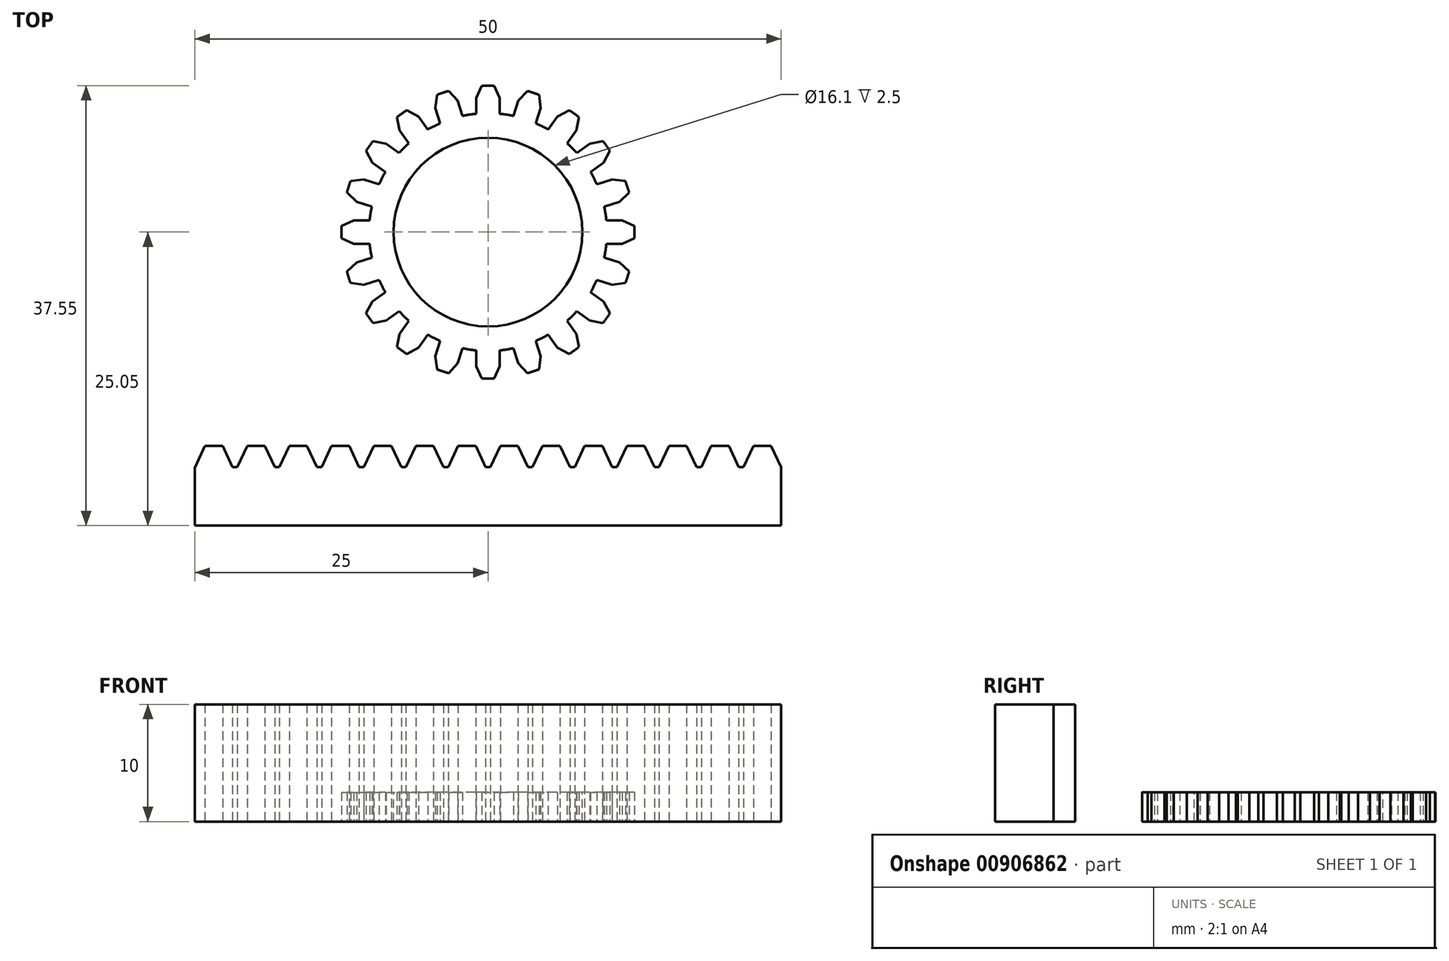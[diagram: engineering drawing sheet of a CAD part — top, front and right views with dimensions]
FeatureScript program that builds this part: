
annotation { "Feature Type Name" : "Feature", "Feature Type Description" : "" }
export const myFeature = defineFeature(function(context is Context, id is Id, definition is map)
    precondition{}
    {
        {
            var Q0;
            Q0=qCreatedBy(makeId("Top.planeOp"),FACE);
            var sketch = newSketch(context, id + "F0", { "sketchPlane" : qUnion([Q0])});
            skCircle(sketch, "E0", {"center": v(0, 0) * mm, "radius": 11.5 * mm, "construction": true});
            skLineSegment(sketch, "E1", {"start": v(-0.52, 12.49) * mm, "end": v(-1, 11.46) * mm});
            skLineSegment(sketch, "E2", {"start": v(-1, 11.46) * mm, "end": v(-1, 10.1) * mm});
            skLineSegment(sketch, "E3", {"start": v(-0.52, 15.02) * mm, "end": v(-0.52, 9.7) * mm, "construction": true});
            skLineSegment(sketch, "E4.MirrorCS", {"start": v(0.52, 12.49) * mm, "end": v(1, 11.46) * mm});
            skLineSegment(sketch, "E5.MirrorCS", {"start": v(1, 11.46) * mm, "end": v(1, 10.1) * mm});
            skArc(sketch, "E6", {"start": v(-0.52, 12.49) * mm, "mid": v(0, 12.5) * mm, "end": v(0.52, 12.49) * mm});
            skLineSegment(sketch, "E7.1.0", {"start": v(-4.5, 10.59) * mm, "end": v(-4.07, 9.3) * mm});
            skLineSegment(sketch, "E7.1.1", {"start": v(-3.37, 12.04) * mm, "end": v(-2.59, 11.2) * mm});
            skLineSegment(sketch, "E7.1.2", {"start": v(-2.59, 11.2) * mm, "end": v(-2.17, 9.91) * mm});
            skLineSegment(sketch, "E7.1.3", {"start": v(-4.35, 11.72) * mm, "end": v(-4.5, 10.59) * mm});
            skArc(sketch, "E7.1.4", {"start": v(-4.35, 11.72) * mm, "mid": v(-3.86, 11.89) * mm, "end": v(-3.37, 12.04) * mm});
            skLineSegment(sketch, "E7.2.0", {"start": v(-7.54, 8.68) * mm, "end": v(-6.74, 7.58) * mm});
            skLineSegment(sketch, "E7.2.1", {"start": v(-6.92, 10.4) * mm, "end": v(-5.92, 9.86) * mm});
            skLineSegment(sketch, "E7.2.2", {"start": v(-5.92, 9.86) * mm, "end": v(-5.13, 8.76) * mm});
            skLineSegment(sketch, "E7.2.3", {"start": v(-7.76, 9.8) * mm, "end": v(-7.54, 8.68) * mm});
            skArc(sketch, "E7.2.4", {"start": v(-7.76, 9.8) * mm, "mid": v(-7.35, 10.11) * mm, "end": v(-6.92, 10.4) * mm});
            skLineSegment(sketch, "E7.3.0", {"start": v(-9.86, 5.92) * mm, "end": v(-8.76, 5.13) * mm});
            skLineSegment(sketch, "E7.3.1", {"start": v(-9.8, 7.76) * mm, "end": v(-8.68, 7.54) * mm});
            skLineSegment(sketch, "E7.3.2", {"start": v(-8.68, 7.54) * mm, "end": v(-7.58, 6.74) * mm});
            skLineSegment(sketch, "E7.3.3", {"start": v(-10.4, 6.92) * mm, "end": v(-9.86, 5.92) * mm});
            skArc(sketch, "E7.3.4", {"start": v(-10.4, 6.92) * mm, "mid": v(-10.11, 7.35) * mm, "end": v(-9.8, 7.76) * mm});
            skLineSegment(sketch, "E7.4.0", {"start": v(-11.2, 2.59) * mm, "end": v(-9.91, 2.17) * mm});
            skLineSegment(sketch, "E7.4.1", {"start": v(-11.72, 4.35) * mm, "end": v(-10.59, 4.5) * mm});
            skLineSegment(sketch, "E7.4.2", {"start": v(-10.59, 4.5) * mm, "end": v(-9.3, 4.07) * mm});
            skLineSegment(sketch, "E7.4.3", {"start": v(-12.04, 3.37) * mm, "end": v(-11.2, 2.59) * mm});
            skArc(sketch, "E7.4.4", {"start": v(-12.04, 3.37) * mm, "mid": v(-11.89, 3.86) * mm, "end": v(-11.72, 4.35) * mm});
            skLineSegment(sketch, "E7.5.0", {"start": v(-11.46, -1) * mm, "end": v(-10.1, -1) * mm});
            skLineSegment(sketch, "E7.5.1", {"start": v(-12.49, 0.52) * mm, "end": v(-11.46, 1) * mm});
            skLineSegment(sketch, "E7.5.2", {"start": v(-11.46, 1) * mm, "end": v(-10.1, 1) * mm});
            skLineSegment(sketch, "E7.5.3", {"start": v(-12.49, -0.52) * mm, "end": v(-11.46, -1) * mm});
            skArc(sketch, "E7.5.4", {"start": v(-12.49, -0.52) * mm, "mid": v(-12.5, 0) * mm, "end": v(-12.49, 0.52) * mm});
            skLineSegment(sketch, "E7.6.0", {"start": v(-10.59, -4.5) * mm, "end": v(-9.3, -4.07) * mm});
            skLineSegment(sketch, "E7.6.1", {"start": v(-12.04, -3.37) * mm, "end": v(-11.2, -2.59) * mm});
            skLineSegment(sketch, "E7.6.2", {"start": v(-11.2, -2.59) * mm, "end": v(-9.91, -2.17) * mm});
            skLineSegment(sketch, "E7.6.3", {"start": v(-11.72, -4.35) * mm, "end": v(-10.59, -4.5) * mm});
            skArc(sketch, "E7.6.4", {"start": v(-11.72, -4.35) * mm, "mid": v(-11.89, -3.86) * mm, "end": v(-12.04, -3.37) * mm});
            skLineSegment(sketch, "E7.7.0", {"start": v(-8.68, -7.54) * mm, "end": v(-7.58, -6.74) * mm});
            skLineSegment(sketch, "E7.7.1", {"start": v(-10.4, -6.92) * mm, "end": v(-9.86, -5.92) * mm});
            skLineSegment(sketch, "E7.7.2", {"start": v(-9.86, -5.92) * mm, "end": v(-8.76, -5.13) * mm});
            skLineSegment(sketch, "E7.7.3", {"start": v(-9.8, -7.76) * mm, "end": v(-8.68, -7.54) * mm});
            skArc(sketch, "E7.7.4", {"start": v(-9.8, -7.76) * mm, "mid": v(-10.11, -7.35) * mm, "end": v(-10.4, -6.92) * mm});
            skLineSegment(sketch, "E7.8.0", {"start": v(-5.92, -9.86) * mm, "end": v(-5.13, -8.76) * mm});
            skLineSegment(sketch, "E7.8.1", {"start": v(-7.76, -9.8) * mm, "end": v(-7.54, -8.68) * mm});
            skLineSegment(sketch, "E7.8.2", {"start": v(-7.54, -8.68) * mm, "end": v(-6.74, -7.58) * mm});
            skLineSegment(sketch, "E7.8.3", {"start": v(-6.92, -10.4) * mm, "end": v(-5.92, -9.86) * mm});
            skArc(sketch, "E7.8.4", {"start": v(-6.92, -10.4) * mm, "mid": v(-7.35, -10.11) * mm, "end": v(-7.76, -9.8) * mm});
            skLineSegment(sketch, "E7.9.0", {"start": v(-2.59, -11.2) * mm, "end": v(-2.17, -9.91) * mm});
            skLineSegment(sketch, "E7.9.1", {"start": v(-4.35, -11.72) * mm, "end": v(-4.5, -10.59) * mm});
            skLineSegment(sketch, "E7.9.2", {"start": v(-4.5, -10.59) * mm, "end": v(-4.07, -9.3) * mm});
            skLineSegment(sketch, "E7.9.3", {"start": v(-3.37, -12.04) * mm, "end": v(-2.59, -11.2) * mm});
            skArc(sketch, "E7.9.4", {"start": v(-3.37, -12.04) * mm, "mid": v(-3.86, -11.89) * mm, "end": v(-4.35, -11.72) * mm});
            skLineSegment(sketch, "E7.10.0", {"start": v(1, -11.46) * mm, "end": v(1, -10.1) * mm});
            skLineSegment(sketch, "E7.10.1", {"start": v(-0.52, -12.49) * mm, "end": v(-1, -11.46) * mm});
            skLineSegment(sketch, "E7.10.2", {"start": v(-1, -11.46) * mm, "end": v(-1, -10.1) * mm});
            skLineSegment(sketch, "E7.10.3", {"start": v(0.52, -12.49) * mm, "end": v(1, -11.46) * mm});
            skArc(sketch, "E7.10.4", {"start": v(0.52, -12.49) * mm, "mid": v(0, -12.5) * mm, "end": v(-0.52, -12.49) * mm});
            skLineSegment(sketch, "E7.11.0", {"start": v(4.5, -10.59) * mm, "end": v(4.07, -9.3) * mm});
            skLineSegment(sketch, "E7.11.1", {"start": v(3.37, -12.04) * mm, "end": v(2.59, -11.2) * mm});
            skLineSegment(sketch, "E7.11.2", {"start": v(2.59, -11.2) * mm, "end": v(2.17, -9.91) * mm});
            skLineSegment(sketch, "E7.11.3", {"start": v(4.35, -11.72) * mm, "end": v(4.5, -10.59) * mm});
            skArc(sketch, "E7.11.4", {"start": v(4.35, -11.72) * mm, "mid": v(3.86, -11.89) * mm, "end": v(3.37, -12.04) * mm});
            skLineSegment(sketch, "E7.12.0", {"start": v(7.54, -8.68) * mm, "end": v(6.74, -7.58) * mm});
            skLineSegment(sketch, "E7.12.1", {"start": v(6.92, -10.4) * mm, "end": v(5.92, -9.86) * mm});
            skLineSegment(sketch, "E7.12.2", {"start": v(5.92, -9.86) * mm, "end": v(5.13, -8.76) * mm});
            skLineSegment(sketch, "E7.12.3", {"start": v(7.76, -9.8) * mm, "end": v(7.54, -8.68) * mm});
            skArc(sketch, "E7.12.4", {"start": v(7.76, -9.8) * mm, "mid": v(7.35, -10.11) * mm, "end": v(6.92, -10.4) * mm});
            skLineSegment(sketch, "E7.13.0", {"start": v(9.86, -5.92) * mm, "end": v(8.76, -5.13) * mm});
            skLineSegment(sketch, "E7.13.1", {"start": v(9.8, -7.76) * mm, "end": v(8.68, -7.54) * mm});
            skLineSegment(sketch, "E7.13.2", {"start": v(8.68, -7.54) * mm, "end": v(7.58, -6.74) * mm});
            skLineSegment(sketch, "E7.13.3", {"start": v(10.4, -6.92) * mm, "end": v(9.86, -5.92) * mm});
            skArc(sketch, "E7.13.4", {"start": v(10.4, -6.92) * mm, "mid": v(10.11, -7.35) * mm, "end": v(9.8, -7.76) * mm});
            skLineSegment(sketch, "E7.14.0", {"start": v(11.2, -2.59) * mm, "end": v(9.91, -2.17) * mm});
            skLineSegment(sketch, "E7.14.1", {"start": v(11.72, -4.35) * mm, "end": v(10.59, -4.5) * mm});
            skLineSegment(sketch, "E7.14.2", {"start": v(10.59, -4.5) * mm, "end": v(9.3, -4.07) * mm});
            skLineSegment(sketch, "E7.14.3", {"start": v(12.04, -3.37) * mm, "end": v(11.2, -2.59) * mm});
            skArc(sketch, "E7.14.4", {"start": v(12.04, -3.37) * mm, "mid": v(11.89, -3.86) * mm, "end": v(11.72, -4.35) * mm});
            skLineSegment(sketch, "E7.15.0", {"start": v(11.46, 1) * mm, "end": v(10.1, 1) * mm});
            skLineSegment(sketch, "E7.15.1", {"start": v(12.49, -0.52) * mm, "end": v(11.46, -1) * mm});
            skLineSegment(sketch, "E7.15.2", {"start": v(11.46, -1) * mm, "end": v(10.1, -1) * mm});
            skLineSegment(sketch, "E7.15.3", {"start": v(12.49, 0.52) * mm, "end": v(11.46, 1) * mm});
            skArc(sketch, "E7.15.4", {"start": v(12.49, 0.52) * mm, "mid": v(12.5, 0) * mm, "end": v(12.49, -0.52) * mm});
            skLineSegment(sketch, "E7.16.0", {"start": v(10.59, 4.5) * mm, "end": v(9.3, 4.07) * mm});
            skLineSegment(sketch, "E7.16.1", {"start": v(12.04, 3.37) * mm, "end": v(11.2, 2.59) * mm});
            skLineSegment(sketch, "E7.16.2", {"start": v(11.2, 2.59) * mm, "end": v(9.91, 2.17) * mm});
            skLineSegment(sketch, "E7.16.3", {"start": v(11.72, 4.35) * mm, "end": v(10.59, 4.5) * mm});
            skArc(sketch, "E7.16.4", {"start": v(11.72, 4.35) * mm, "mid": v(11.89, 3.86) * mm, "end": v(12.04, 3.37) * mm});
            skLineSegment(sketch, "E7.17.0", {"start": v(8.68, 7.54) * mm, "end": v(7.58, 6.74) * mm});
            skLineSegment(sketch, "E7.17.1", {"start": v(10.4, 6.92) * mm, "end": v(9.86, 5.92) * mm});
            skLineSegment(sketch, "E7.17.2", {"start": v(9.86, 5.92) * mm, "end": v(8.76, 5.13) * mm});
            skLineSegment(sketch, "E7.17.3", {"start": v(9.8, 7.76) * mm, "end": v(8.68, 7.54) * mm});
            skArc(sketch, "E7.17.4", {"start": v(9.8, 7.76) * mm, "mid": v(10.11, 7.35) * mm, "end": v(10.4, 6.92) * mm});
            skLineSegment(sketch, "E7.18.0", {"start": v(5.92, 9.86) * mm, "end": v(5.13, 8.76) * mm});
            skLineSegment(sketch, "E7.18.1", {"start": v(7.76, 9.8) * mm, "end": v(7.54, 8.68) * mm});
            skLineSegment(sketch, "E7.18.2", {"start": v(7.54, 8.68) * mm, "end": v(6.74, 7.58) * mm});
            skLineSegment(sketch, "E7.18.3", {"start": v(6.92, 10.4) * mm, "end": v(5.92, 9.86) * mm});
            skArc(sketch, "E7.18.4", {"start": v(6.92, 10.4) * mm, "mid": v(7.35, 10.11) * mm, "end": v(7.76, 9.8) * mm});
            skLineSegment(sketch, "E7.19.0", {"start": v(2.59, 11.2) * mm, "end": v(2.17, 9.91) * mm});
            skLineSegment(sketch, "E7.19.1", {"start": v(4.35, 11.72) * mm, "end": v(4.5, 10.59) * mm});
            skLineSegment(sketch, "E7.19.2", {"start": v(4.5, 10.59) * mm, "end": v(4.07, 9.3) * mm});
            skLineSegment(sketch, "E7.19.3", {"start": v(3.37, 12.04) * mm, "end": v(2.59, 11.2) * mm});
            skArc(sketch, "E7.19.4", {"start": v(3.37, 12.04) * mm, "mid": v(3.86, 11.89) * mm, "end": v(4.35, 11.72) * mm});
            skArc(sketch, "E8", {"start": v(-4.07, 9.3) * mm, "mid": v(-4.6, 9.04) * mm, "end": v(-5.13, 8.76) * mm});
            skArc(sketch, "E9.trimOffspring", {"start": v(-6.74, 7.58) * mm, "mid": v(-7.17, 7.17) * mm, "end": v(-7.58, 6.74) * mm});
            skArc(sketch, "E10.trimOffspring", {"start": v(-8.76, 5.13) * mm, "mid": v(-9.04, 4.6) * mm, "end": v(-9.3, 4.07) * mm});
            skArc(sketch, "E11.trimOffspring", {"start": v(-9.91, 2.17) * mm, "mid": v(-10.02, 1.59) * mm, "end": v(-10.1, 1) * mm});
            skArc(sketch, "E12.trimOffspring", {"start": v(-10.1, -1) * mm, "mid": v(-10.02, -1.59) * mm, "end": v(-9.91, -2.17) * mm});
            skArc(sketch, "E13.trimOffspring", {"start": v(-9.3, -4.07) * mm, "mid": v(-9.04, -4.6) * mm, "end": v(-8.76, -5.13) * mm});
            skArc(sketch, "E14.trimOffspring", {"start": v(-7.58, -6.74) * mm, "mid": v(-7.17, -7.17) * mm, "end": v(-6.74, -7.58) * mm});
            skArc(sketch, "E15.trimOffspring", {"start": v(-5.13, -8.76) * mm, "mid": v(-4.6, -9.04) * mm, "end": v(-4.07, -9.3) * mm});
            skArc(sketch, "E16.trimOffspring", {"start": v(-2.17, -9.91) * mm, "mid": v(-1.59, -10.02) * mm, "end": v(-1, -10.1) * mm});
            skArc(sketch, "E17.trimOffspring", {"start": v(1, -10.1) * mm, "mid": v(1.59, -10.02) * mm, "end": v(2.17, -9.91) * mm});
            skArc(sketch, "E18.trimOffspring", {"start": v(4.07, -9.3) * mm, "mid": v(4.6, -9.04) * mm, "end": v(5.13, -8.76) * mm});
            skArc(sketch, "E19.trimOffspring", {"start": v(6.74, -7.58) * mm, "mid": v(7.17, -7.17) * mm, "end": v(7.58, -6.74) * mm});
            skArc(sketch, "E20.trimOffspring", {"start": v(8.76, -5.13) * mm, "mid": v(9.04, -4.6) * mm, "end": v(9.3, -4.07) * mm});
            skArc(sketch, "E21.trimOffspring", {"start": v(9.91, -2.17) * mm, "mid": v(10.02, -1.59) * mm, "end": v(10.1, -1) * mm});
            skArc(sketch, "E22.trimOffspring", {"start": v(10.1, 1) * mm, "mid": v(10.02, 1.59) * mm, "end": v(9.91, 2.17) * mm});
            skArc(sketch, "E23.trimOffspring", {"start": v(9.3, 4.07) * mm, "mid": v(9.04, 4.6) * mm, "end": v(8.76, 5.13) * mm});
            skArc(sketch, "E24.trimOffspring", {"start": v(7.58, 6.74) * mm, "mid": v(7.17, 7.17) * mm, "end": v(6.74, 7.58) * mm});
            skArc(sketch, "E25.trimOffspring", {"start": v(5.13, 8.76) * mm, "mid": v(4.6, 9.04) * mm, "end": v(4.07, 9.3) * mm});
            skArc(sketch, "E26.trimOffspring", {"start": v(2.17, 9.91) * mm, "mid": v(1.59, 10.02) * mm, "end": v(1, 10.1) * mm});
            skArc(sketch, "E27.trimOffspring", {"start": v(-0.52, 10.13) * mm, "mid": v(-1.35, 10.06) * mm, "end": v(-2.17, 9.91) * mm});
            skSolve(sketch);
        }
        {
            var Q0;
            Q0 = qSketchRegion(id + "F0", true);
            extrude(context, id + "F1", {"entities" : qUnion([Q0]), "depth" : 2.5 * mm, "offsetDistance" : 25 * mm});
        }
        {
            var Q0;
            Q0=makeQuery(id+"F1.opExtrude","CAP_FACE",FACE,{"disambiguationData":[OSD([sQuery(id+"F0.wireOp",EDGE,"E1"),sQuery(id+"F0.wireOp",EDGE,"E2"),sQuery(id+"F0.wireOp",EDGE,"E4.MirrorCS"),sQuery(id+"F0.wireOp",EDGE,"E5.MirrorCS"),sQuery(id+"F0.wireOp",EDGE,"E6"),sQuery(id+"F0.wireOp",EDGE,"E7.1.0"),sQuery(id+"F0.wireOp",EDGE,"E7.1.1"),sQuery(id+"F0.wireOp",EDGE,"E7.1.2"),sQuery(id+"F0.wireOp",EDGE,"E7.1.3"),sQuery(id+"F0.wireOp",EDGE,"E7.1.4"),sQuery(id+"F0.wireOp",EDGE,"E7.2.0"),sQuery(id+"F0.wireOp",EDGE,"E7.2.1"),sQuery(id+"F0.wireOp",EDGE,"E7.2.2"),sQuery(id+"F0.wireOp",EDGE,"E7.2.3"),sQuery(id+"F0.wireOp",EDGE,"E7.2.4"),sQuery(id+"F0.wireOp",EDGE,"E7.3.0"),sQuery(id+"F0.wireOp",EDGE,"E7.3.1"),sQuery(id+"F0.wireOp",EDGE,"E7.3.2"),sQuery(id+"F0.wireOp",EDGE,"E7.3.3"),sQuery(id+"F0.wireOp",EDGE,"E7.3.4"),sQuery(id+"F0.wireOp",EDGE,"E7.4.0"),sQuery(id+"F0.wireOp",EDGE,"E7.4.1"),sQuery(id+"F0.wireOp",EDGE,"E7.4.2"),sQuery(id+"F0.wireOp",EDGE,"E7.4.3"),sQuery(id+"F0.wireOp",EDGE,"E7.4.4"),sQuery(id+"F0.wireOp",EDGE,"E7.5.0"),sQuery(id+"F0.wireOp",EDGE,"E7.5.1"),sQuery(id+"F0.wireOp",EDGE,"E7.5.2"),sQuery(id+"F0.wireOp",EDGE,"E7.5.3"),sQuery(id+"F0.wireOp",EDGE,"E7.5.4"),sQuery(id+"F0.wireOp",EDGE,"E7.6.0"),sQuery(id+"F0.wireOp",EDGE,"E7.6.1"),sQuery(id+"F0.wireOp",EDGE,"E7.6.2"),sQuery(id+"F0.wireOp",EDGE,"E7.6.3"),sQuery(id+"F0.wireOp",EDGE,"E7.6.4"),sQuery(id+"F0.wireOp",EDGE,"E7.7.0"),sQuery(id+"F0.wireOp",EDGE,"E7.7.1"),sQuery(id+"F0.wireOp",EDGE,"E7.7.2"),sQuery(id+"F0.wireOp",EDGE,"E7.7.3"),sQuery(id+"F0.wireOp",EDGE,"E7.7.4"),sQuery(id+"F0.wireOp",EDGE,"E7.8.0"),sQuery(id+"F0.wireOp",EDGE,"E7.8.1"),sQuery(id+"F0.wireOp",EDGE,"E7.8.2"),sQuery(id+"F0.wireOp",EDGE,"E7.8.3"),sQuery(id+"F0.wireOp",EDGE,"E7.8.4"),sQuery(id+"F0.wireOp",EDGE,"E7.9.0"),sQuery(id+"F0.wireOp",EDGE,"E7.9.1"),sQuery(id+"F0.wireOp",EDGE,"E7.9.2"),sQuery(id+"F0.wireOp",EDGE,"E7.9.3"),sQuery(id+"F0.wireOp",EDGE,"E7.9.4"),sQuery(id+"F0.wireOp",EDGE,"E7.10.0"),sQuery(id+"F0.wireOp",EDGE,"E7.10.1"),sQuery(id+"F0.wireOp",EDGE,"E7.10.2"),sQuery(id+"F0.wireOp",EDGE,"E7.10.3"),sQuery(id+"F0.wireOp",EDGE,"E7.10.4"),sQuery(id+"F0.wireOp",EDGE,"E7.11.0"),sQuery(id+"F0.wireOp",EDGE,"E7.11.1"),sQuery(id+"F0.wireOp",EDGE,"E7.11.2"),sQuery(id+"F0.wireOp",EDGE,"E7.11.3"),sQuery(id+"F0.wireOp",EDGE,"E7.11.4"),sQuery(id+"F0.wireOp",EDGE,"E7.12.0"),sQuery(id+"F0.wireOp",EDGE,"E7.12.1"),sQuery(id+"F0.wireOp",EDGE,"E7.12.2"),sQuery(id+"F0.wireOp",EDGE,"E7.12.3"),sQuery(id+"F0.wireOp",EDGE,"E7.12.4"),sQuery(id+"F0.wireOp",EDGE,"E7.13.0"),sQuery(id+"F0.wireOp",EDGE,"E7.13.1"),sQuery(id+"F0.wireOp",EDGE,"E7.13.2"),sQuery(id+"F0.wireOp",EDGE,"E7.13.3"),sQuery(id+"F0.wireOp",EDGE,"E7.13.4"),sQuery(id+"F0.wireOp",EDGE,"E7.14.0"),sQuery(id+"F0.wireOp",EDGE,"E7.14.1"),sQuery(id+"F0.wireOp",EDGE,"E7.14.2"),sQuery(id+"F0.wireOp",EDGE,"E7.14.3"),sQuery(id+"F0.wireOp",EDGE,"E7.14.4"),sQuery(id+"F0.wireOp",EDGE,"E7.15.0"),sQuery(id+"F0.wireOp",EDGE,"E7.15.1"),sQuery(id+"F0.wireOp",EDGE,"E7.15.2"),sQuery(id+"F0.wireOp",EDGE,"E7.15.3"),sQuery(id+"F0.wireOp",EDGE,"E7.15.4"),sQuery(id+"F0.wireOp",EDGE,"E7.16.0"),sQuery(id+"F0.wireOp",EDGE,"E7.16.1"),sQuery(id+"F0.wireOp",EDGE,"E7.16.2"),sQuery(id+"F0.wireOp",EDGE,"E7.16.3"),sQuery(id+"F0.wireOp",EDGE,"E7.16.4"),sQuery(id+"F0.wireOp",EDGE,"E7.17.0"),sQuery(id+"F0.wireOp",EDGE,"E7.17.1"),sQuery(id+"F0.wireOp",EDGE,"E7.17.2"),sQuery(id+"F0.wireOp",EDGE,"E7.17.3"),sQuery(id+"F0.wireOp",EDGE,"E7.17.4"),sQuery(id+"F0.wireOp",EDGE,"E7.18.0"),sQuery(id+"F0.wireOp",EDGE,"E7.18.1"),sQuery(id+"F0.wireOp",EDGE,"E7.18.2"),sQuery(id+"F0.wireOp",EDGE,"E7.18.3"),sQuery(id+"F0.wireOp",EDGE,"E7.18.4"),sQuery(id+"F0.wireOp",EDGE,"E7.19.0"),sQuery(id+"F0.wireOp",EDGE,"E7.19.1"),sQuery(id+"F0.wireOp",EDGE,"E7.19.2"),sQuery(id+"F0.wireOp",EDGE,"E7.19.3"),sQuery(id+"F0.wireOp",EDGE,"E7.19.4"),sQuery(id+"F0.wireOp",EDGE,"E8"),sQuery(id+"F0.wireOp",EDGE,"E9.trimOffspring"),sQuery(id+"F0.wireOp",EDGE,"E10.trimOffspring"),sQuery(id+"F0.wireOp",EDGE,"E11.trimOffspring"),sQuery(id+"F0.wireOp",EDGE,"E12.trimOffspring"),sQuery(id+"F0.wireOp",EDGE,"E13.trimOffspring"),sQuery(id+"F0.wireOp",EDGE,"E14.trimOffspring"),sQuery(id+"F0.wireOp",EDGE,"E15.trimOffspring"),sQuery(id+"F0.wireOp",EDGE,"E16.trimOffspring"),sQuery(id+"F0.wireOp",EDGE,"E17.trimOffspring"),sQuery(id+"F0.wireOp",EDGE,"E18.trimOffspring"),sQuery(id+"F0.wireOp",EDGE,"E19.trimOffspring"),sQuery(id+"F0.wireOp",EDGE,"E20.trimOffspring"),sQuery(id+"F0.wireOp",EDGE,"E21.trimOffspring"),sQuery(id+"F0.wireOp",EDGE,"E22.trimOffspring"),sQuery(id+"F0.wireOp",EDGE,"E23.trimOffspring"),sQuery(id+"F0.wireOp",EDGE,"E24.trimOffspring"),sQuery(id+"F0.wireOp",EDGE,"E25.trimOffspring"),sQuery(id+"F0.wireOp",EDGE,"E26.trimOffspring"),sQuery(id+"F0.wireOp",EDGE,"E27.trimOffspring")])],"isStart":false});
            var sketch = newSketch(context, id + "F2", { "sketchPlane" : qUnion([Q0])});
            skCircle(sketch, "E28", {"center": v(0, 0) * mm, "radius": 8.05 * mm});
            skSolve(sketch);
        }
        {
            var Q0;
            Q0 = qSketchRegion(id + "F2", true);
            extrude(context, id + "F3", {"entities" : qUnion([Q0]), "operationType" : NewBodyOperationType.REMOVE, "endBound" : BoundingType.THROUGH_ALL, "oppositeDirection" : true, "depth" : 25 * mm, "offsetDistance" : 25 * mm});
        }
        {
            var Q0;
            Q0=qCreatedBy(makeId("Top.planeOp"),FACE);
            var sketch = newSketch(context, id + "F4", { "sketchPlane" : qUnion([Q0])});
            skLineSegment(sketch, "E29.bottom", {"start": v(-25, -20.05) * mm, "end": v(25, -20.05) * mm});
            skLineSegment(sketch, "E29.top", {"start": v(-25, -25.05) * mm, "end": v(25, -25.05) * mm});
            skLineSegment(sketch, "E29.left", {"start": v(-25, -20.05) * mm, "end": v(-25, -25.05) * mm});
            skLineSegment(sketch, "E29.right", {"start": v(25, -20.05) * mm, "end": v(25, -25.05) * mm});
            skLineSegment(sketch, "E30", {"start": v(-3.4, -20.05) * mm, "end": v(-3.4, -20.05) * mm});
            skLineSegment(sketch, "E31", {"start": v(-3.4, -20.05) * mm, "end": v(-2.55, -18.24) * mm});
            skLineSegment(sketch, "E32", {"start": v(-2.55, -18.24) * mm, "end": v(-1.05, -18.24) * mm});
            skLineSegment(sketch, "E33", {"start": v(-1.05, -18.24) * mm, "end": v(-0.2, -20.05) * mm});
            skLineSegment(sketch, "E34", {"start": v(-0.2, -20.05) * mm, "end": v(-0.2, -20.05) * mm});
            skLineSegment(sketch, "E35", {"start": v(-1.05, -18.24) * mm, "end": v(-1.05, -28.83) * mm, "construction": true});
            skLineSegment(sketch, "E36", {"start": v(-2.55, -18.24) * mm, "end": v(-2.55, -28.87) * mm, "construction": true});
            skLineSegment(sketch, "E37.MirrorCS", {"start": v(1.05, -18.24) * mm, "end": v(0.2, -20.05) * mm});
            skLineSegment(sketch, "E38.MirrorCS", {"start": v(0.2, -20.05) * mm, "end": v(0.2, -20.05) * mm});
            skLineSegment(sketch, "E39.MirrorCS", {"start": v(3.4, -20.05) * mm, "end": v(3.4, -20.05) * mm});
            skLineSegment(sketch, "E40.MirrorCS", {"start": v(2.55, -18.24) * mm, "end": v(1.05, -18.24) * mm});
            skLineSegment(sketch, "E41.MirrorCS", {"start": v(3.4, -20.05) * mm, "end": v(2.55, -18.24) * mm});
            skLineSegment(sketch, "E42", {"start": v(-25.16, -20.05) * mm, "end": v(25.29, -20.05) * mm, "construction": true});
            skLineSegment(sketch, "E43.1.0.0", {"start": v(6.15, -18.24) * mm, "end": v(7, -20.05) * mm});
            skLineSegment(sketch, "E43.1.0.1", {"start": v(3.8, -20.05) * mm, "end": v(4.65, -18.24) * mm});
            skLineSegment(sketch, "E43.1.0.2", {"start": v(8.24, -18.24) * mm, "end": v(7.4, -20.05) * mm});
            skLineSegment(sketch, "E43.1.0.3", {"start": v(9.74, -18.24) * mm, "end": v(8.24, -18.24) * mm});
            skLineSegment(sketch, "E43.1.0.4", {"start": v(10.6, -20.05) * mm, "end": v(9.74, -18.24) * mm});
            skLineSegment(sketch, "E43.1.0.5", {"start": v(4.65, -18.24) * mm, "end": v(6.15, -18.24) * mm});
            skLineSegment(sketch, "E43.2.0.0", {"start": v(13.34, -18.24) * mm, "end": v(14.19, -20.05) * mm});
            skLineSegment(sketch, "E43.2.0.1", {"start": v(11, -20.05) * mm, "end": v(11.84, -18.24) * mm});
            skLineSegment(sketch, "E43.2.0.5", {"start": v(11.84, -18.24) * mm, "end": v(13.34, -18.24) * mm});
            skLineSegment(sketch, "E43.direction1", {"start": v(-3.4, -20.05) * mm, "end": v(3.8, -20.05) * mm, "construction": true});
            skLineSegment(sketch, "E44", {"start": v(-14.19, -20.05) * mm, "end": v(-13.34, -18.24) * mm});
            skLineSegment(sketch, "E45", {"start": v(-13.34, -18.24) * mm, "end": v(-11.84, -18.24) * mm});
            skLineSegment(sketch, "E46", {"start": v(-11.84, -18.24) * mm, "end": v(-11, -20.05) * mm});
            skLineSegment(sketch, "E47", {"start": v(-7, -20.05) * mm, "end": v(-6.15, -18.24) * mm});
            skLineSegment(sketch, "E48", {"start": v(-6.15, -18.24) * mm, "end": v(-4.65, -18.24) * mm});
            skLineSegment(sketch, "E49", {"start": v(-4.65, -18.24) * mm, "end": v(-3.8, -20.05) * mm});
            skLineSegment(sketch, "E50", {"start": v(-10.6, -20.05) * mm, "end": v(-9.74, -18.24) * mm});
            skLineSegment(sketch, "E51", {"start": v(-9.74, -18.24) * mm, "end": v(-8.24, -18.24) * mm});
            skLineSegment(sketch, "E52", {"start": v(-8.24, -18.24) * mm, "end": v(-7.4, -20.05) * mm});
            skLineSegment(sketch, "E53", {"start": v(-29.2, -18.86) * mm, "end": v(28.44, -18.86) * mm, "construction": true});
            skPoint(sketch, "E54", {"position": v(2.84, -18.86) * mm});
            skLineSegment(sketch, "E55", {"start": v(-17.79, -20.05) * mm, "end": v(-16.94, -18.24) * mm});
            skLineSegment(sketch, "E56", {"start": v(-16.94, -18.24) * mm, "end": v(-15.44, -18.24) * mm});
            skLineSegment(sketch, "E57", {"start": v(-15.44, -18.24) * mm, "end": v(-14.6, -20.05) * mm});
            skLineSegment(sketch, "E58", {"start": v(-21.38, -20.05) * mm, "end": v(-20.54, -18.24) * mm});
            skLineSegment(sketch, "E59", {"start": v(-20.54, -18.24) * mm, "end": v(-19.04, -18.24) * mm});
            skLineSegment(sketch, "E60", {"start": v(-19.04, -18.24) * mm, "end": v(-18.2, -20.05) * mm});
            skLineSegment(sketch, "E61", {"start": v(-24.98, -20.05) * mm, "end": v(-24.14, -18.24) * mm});
            skLineSegment(sketch, "E62", {"start": v(-24.14, -18.24) * mm, "end": v(-22.64, -18.24) * mm});
            skLineSegment(sketch, "E63", {"start": v(-22.64, -18.24) * mm, "end": v(-21.8, -20.05) * mm});
            skLineSegment(sketch, "E64", {"start": v(18.74, -18.6) * mm, "end": v(18.74, -18.6) * mm});
            skLineSegment(sketch, "E65", {"start": v(18.2, -20.05) * mm, "end": v(19.04, -18.24) * mm});
            skLineSegment(sketch, "E66", {"start": v(19.04, -18.24) * mm, "end": v(20.54, -18.24) * mm});
            skLineSegment(sketch, "E67", {"start": v(20.54, -18.24) * mm, "end": v(21.38, -20.05) * mm});
            skLineSegment(sketch, "E68", {"start": v(21.8, -20.05) * mm, "end": v(22.64, -18.24) * mm});
            skLineSegment(sketch, "E69", {"start": v(22.64, -18.24) * mm, "end": v(24.14, -18.24) * mm});
            skLineSegment(sketch, "E70", {"start": v(24.14, -18.24) * mm, "end": v(24.98, -20.05) * mm});
            skLineSegment(sketch, "E71", {"start": v(17.38, -20.22) * mm, "end": v(17.38, -20.22) * mm});
            skLineSegment(sketch, "E72", {"start": v(14.6, -20.05) * mm, "end": v(15.44, -18.24) * mm});
            skLineSegment(sketch, "E73", {"start": v(15.44, -18.24) * mm, "end": v(16.94, -18.24) * mm});
            skLineSegment(sketch, "E74", {"start": v(16.94, -18.24) * mm, "end": v(17.79, -20.05) * mm});
            skLineSegment(sketch, "E75", {"start": v(20.57, -20.22) * mm, "end": v(20.57, -20.22) * mm});
            skSolve(sketch);
        }
        {
            var Q0;
            Q0 = qSketchRegion(id + "F4", true);
            extrude(context, id + "F5", {"entities" : qUnion([Q0]), "depth" : 10 * mm, "offsetDistance" : 25 * mm});
        }
    });
